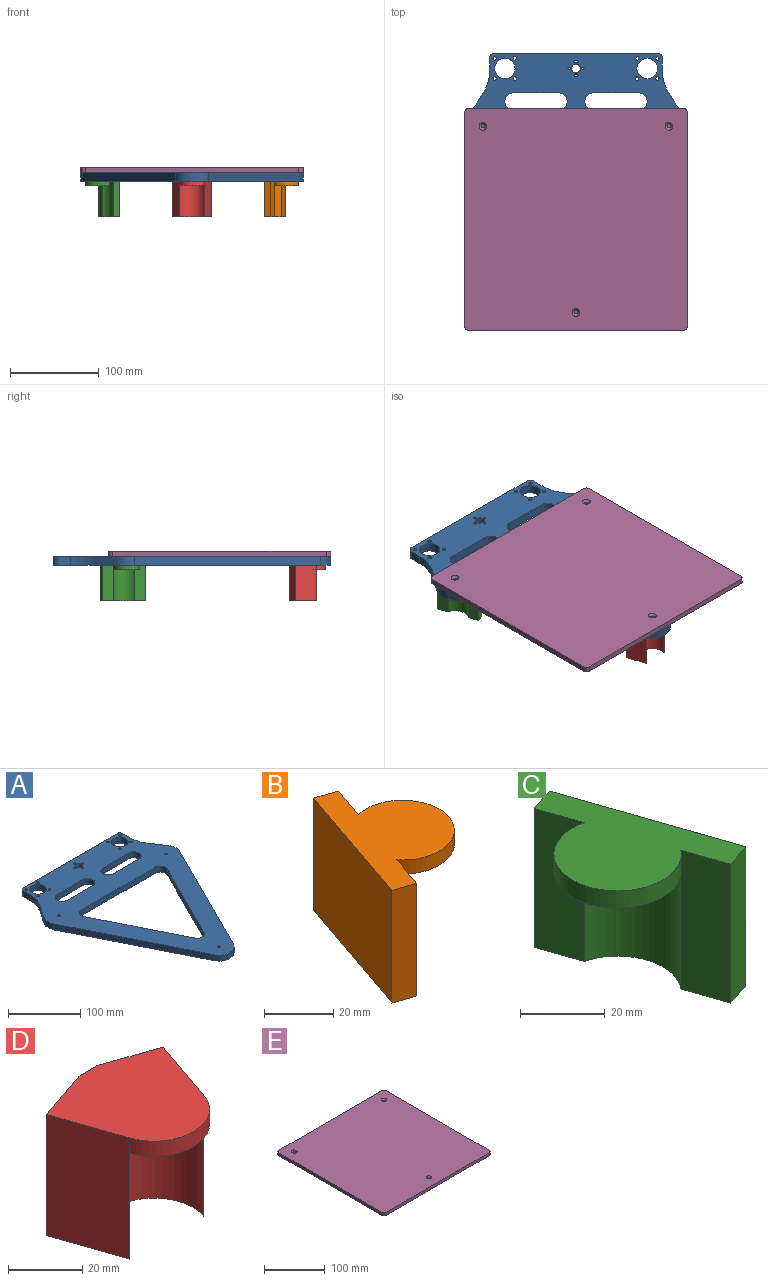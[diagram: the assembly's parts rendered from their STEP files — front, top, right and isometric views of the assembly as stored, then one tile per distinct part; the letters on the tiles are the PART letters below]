
ASSEMBLY  parts=5 mates=4
PART A: 48 faces, bbox 250x311.5x10 mm
  f0: plane 184x10mm, normal (0,1,0), area 1840mm2, adj f1,f13,f46,f47
  f1: cylinder r=5mm len=10mm, axis (0,0,-1), area 78.5mm2, adj f0,f2,f46,f47
  f2: plane 13.79x10mm, normal (-1,0,0), area 137.9mm2, adj f1,f3,f46,f47
  f3: cylinder r=50mm len=27.84mm, axis (0,0,-1), area 295.3mm2, adj f2,f4,f46,f47
  f4: plane 23.95x16.06mm, normal (-0.83,0.56,0), area 288.4mm2, adj f3,f5,f46,f47
  f5: cylinder r=20.5mm len=20.58mm, axis (0,0,-1), area 216.1mm2, adj f4,f6,f46,f47
  f6: plane 209x104.5mm, normal (-0.89,-0.45,0), area 2336.7mm2, adj f5,f7,f46,f47
  f7: cylinder r=20.5mm len=36.67mm, axis (0,0,-1), area 453.9mm2, adj f6,f8,f46,f47
  f8: plane 209x104.5mm, normal (0.89,-0.45,0), area 2336.7mm2, adj f7,f9,f46,f47
  f9: cylinder r=20.5mm len=20.58mm, axis (0,0,-1), area 216.1mm2, adj f8,f10,f46,f47
  f10: plane 23.95x16.06mm, normal (0.83,0.56,0), area 288.4mm2, adj f9,f11,f46,f47
  f11: cylinder r=50mm len=27.84mm, axis (0,0,-1), area 295.3mm2, adj f10,f12,f46,f47
  f12: plane 13.79x10mm, normal (1,0,0), area 137.9mm2, adj f11,f13,f46,f47
  f13: cylinder r=5mm len=10mm, axis (0,0,-1), area 78.5mm2, adj f0,f12,f46,f47
  f14: cylinder r=10mm len=14.47mm, axis (0,0,-1), area 203.4mm2, adj f15,f25,f46,f47
  f15: plane 143.84x71.92mm, normal (-0.89,0.45,0), area 1608.2mm2, adj f14,f16,f46,f47
  f16: cylinder r=10mm len=17.89mm, axis (0,0,-1), area 221.4mm2, adj f15,f17,f46,f47
  f17: plane 143.84x71.92mm, normal (0.89,0.45,0), area 1608.2mm2, adj f16,f18,f46,f47
  f18: cylinder r=10mm len=14.47mm, axis (0,0,-1), area 203.4mm2, adj f17,f25,f46,f47
  f19: plane 50x10mm, normal (0,1,0), area 500mm2, adj f20,f26,f46,f47
  f20: cylinder r=10mm len=20mm, axis (0,0,-1), area 314.2mm2, adj f19,f21,f46,f47
  f21: plane 50x10mm, normal (0,-1,0), area 500mm2, adj f20,f26,f46,f47
  f22: cylinder r=10mm len=20mm, axis (0,0,-1), area 314.2mm2, adj f23,f27,f46,f47
  f23: plane 50x10mm, normal (0,-1,0), area 500mm2, adj f22,f24,f46,f47
  f24: cylinder r=10mm len=20mm, axis (0,0,-1), area 314.2mm2, adj f23,f27,f46,f47
  f25: plane 143.84x10mm, normal (0,-1,0), area 1438.4mm2, adj f14,f18,f46,f47
  f26: cylinder r=10mm len=20mm, axis (0,0,-1), area 314.2mm2, adj f19,f21,f46,f47
  f27: plane 50x10mm, normal (0,1,0), area 500mm2, adj f22,f24,f46,f47
  f28: cylinder r=11.5mm len=23mm, axis (0,0,-1), area 722.6mm2, adj f46,f47
  f29: cylinder r=11.5mm len=23mm, axis (0,0,-1), area 722.6mm2, adj f46,f47
  f30: cylinder r=2mm len=10mm, axis (0,0,-1), area 125.7mm2, adj f46,f47
  f31: cylinder r=2mm len=10mm, axis (0,0,-1), area 125.7mm2, adj f46,f47
  f32: cylinder r=2mm len=10mm, axis (0,0,-1), area 125.7mm2, adj f46,f47
  f33: cylinder r=2mm len=10mm, axis (0,0,-1), area 125.7mm2, adj f46,f47
  f34: cylinder r=2mm len=10mm, axis (0,0,-1), area 125.7mm2, adj f46,f47
  f35: cylinder r=2mm len=10mm, axis (0,0,-1), area 125.7mm2, adj f46,f47
  f36: cylinder r=2mm len=10mm, axis (0,0,-1), area 125.7mm2, adj f46,f47
  f37: cylinder r=2mm len=10mm, axis (0,0,-1), area 125.7mm2, adj f46,f47
  f38: cylinder r=2mm len=10mm, axis (0,0,-1), area 125.7mm2, adj f46,f47
  f39: cylinder r=2mm len=10mm, axis (0,0,-1), area 125.7mm2, adj f46,f47
  f40: cylinder r=2mm len=10mm, axis (0,0,-1), area 125.7mm2, adj f46,f47
  f41: cylinder r=5mm len=10mm, axis (0,0,-1), area 314.2mm2, adj f46,f47
  f42: cylinder r=1.5mm len=10mm, axis (0,0,-1), area 94.2mm2, adj f46,f47
  f43: cylinder r=1.5mm len=10mm, axis (0,0,-1), area 94.2mm2, adj f46,f47
  f44: cylinder r=1.5mm len=10mm, axis (0,0,-1), area 94.2mm2, adj f46,f47
  f45: cylinder r=1.5mm len=10mm, axis (0,0,-1), area 94.2mm2, adj f46,f47
  f46: plane 311.5x250mm, normal (0,0,1), area 30515.8mm2, adj f0,f1,f2,f3,f4,f5,f6,f7
  f47: plane 311.5x250mm, normal (0,0,-1), area 30515.8mm2, adj f0,f1,f2,f3,f4,f5,f6,f7
PART B: 10 faces, bbox 38.5x51.4x40 mm
  f0: cylinder r=15mm len=30mm, axis (0,0,1), area 320mm2, adj f1,f2,f4,f8
  f1: plane 30x30mm, normal (0,0,-1), area 706.9mm2, adj f0,f3
  f2: plane 51.38x38.5mm, normal (0,0,1), area 994.1mm2, adj f0,f4,f5,f6,f7,f8
  f3: cylinder r=15mm len=35mm, axis (0,0,1), area 1058.7mm2, adj f1,f4,f8,f9
  f4: plane 40x12.39mm, normal (0.95,-0.32,0), area 524mm2, adj f0,f2,f3,f5,f9
  f5: plane 40x7.57mm, normal (0.32,0.95,0), area 320mm2, adj f2,f4,f6,f9
  f6: plane 48.78x40mm, normal (-0.95,0.32,0), area 2063mm2, adj f2,f5,f7,f9
  f7: plane 40x7.57mm, normal (-0.32,-0.95,0), area 320mm2, adj f2,f6,f8,f9
  f8: plane 40x12.39mm, normal (0.95,-0.32,0), area 524mm2, adj f0,f2,f3,f7,f9
  f9: plane 51.38x24.31mm, normal (0,0,-1), area 287.3mm2, adj f3,f4,f5,f6,f7,f8
PART C: 10 faces, bbox 38.5x51.4x40 mm
  f0: cylinder r=15mm len=30mm, axis (0,0,1), area 320mm2, adj f1,f2,f4,f5
  f1: plane 30x30mm, normal (0,0,-1), area 706.9mm2, adj f0,f3
  f2: plane 51.38x38.5mm, normal (0,0,1), area 994.1mm2, adj f0,f4,f5,f6,f7,f8
  f3: cylinder r=15mm len=35mm, axis (0,0,1), area 1058.7mm2, adj f1,f4,f5,f9
  f4: plane 40x12.39mm, normal (-0.95,-0.32,0), area 524mm2, adj f0,f2,f3,f8,f9
  f5: plane 40x12.39mm, normal (-0.95,-0.32,0), area 524mm2, adj f0,f2,f3,f6,f9
  f6: plane 40x7.57mm, normal (0.32,-0.95,0), area 320mm2, adj f2,f5,f7,f9
  f7: plane 48.78x40mm, normal (0.95,0.32,0), area 2063mm2, adj f2,f6,f8,f9
  f8: plane 40x7.57mm, normal (-0.32,0.95,0), area 320mm2, adj f2,f4,f7,f9
  f9: plane 51.38x24.31mm, normal (0,0,-1), area 287.3mm2, adj f3,f4,f5,f6,f7,f8
PART D: 10 faces, bbox 44.6x40.3x40 mm
  f0: plane 30x30mm, normal (0,0,-1), area 706.9mm2, adj f1,f8
  f1: cylinder r=15mm len=28.38mm, axis (0,0,1), area 186mm2, adj f0,f2,f6,f7
  f2: plane 40x23.65mm, normal (0.95,-0.32,0), area 1000mm2, adj f1,f3,f7,f8,f9
  f3: plane 40x18.92mm, normal (0.32,0.95,0), area 800mm2, adj f2,f4,f7,f9
  f4: plane 40x6.77mm, normal (0,1,0), area 270.9mm2, adj f3,f5,f7,f9
  f5: plane 40x18.92mm, normal (-0.32,0.95,0), area 800mm2, adj f4,f6,f7,f9
  f6: plane 40x23.65mm, normal (-0.95,-0.32,0), area 1000mm2, adj f1,f5,f7,f8,f9
  f7: plane 44.61x40.27mm, normal (0,0,1), area 1239.6mm2, adj f1,f2,f3,f4,f5,f6
  f8: cylinder r=15mm len=35mm, axis (0,0,1), area 1996.5mm2, adj f0,f2,f6,f9
  f9: plane 44.61x30.14mm, normal (0,0,-1), area 532.7mm2, adj f2,f3,f4,f5,f6,f8
PART E: 16 faces, bbox 250x250x6 mm
  f0: cylinder r=5mm len=6mm, axis (0,0,1), area 47.1mm2, adj f1,f7,f8,f9
  f1: plane 240x6mm, normal (0,-1,0), area 1440mm2, adj f0,f2,f8,f9
  f2: cylinder r=5mm len=6mm, axis (0,0,1), area 47.1mm2, adj f1,f3,f8,f9
  f3: plane 240x6mm, normal (1,0,0), area 1440mm2, adj f2,f4,f8,f9
  f4: cylinder r=5mm len=6mm, axis (0,0,1), area 47.1mm2, adj f3,f5,f8,f9
  f5: plane 240x6mm, normal (0,1,0), area 1440mm2, adj f4,f6,f8,f9
  f6: cylinder r=5mm len=6mm, axis (0,0,1), area 47.1mm2, adj f5,f7,f8,f9
  f7: plane 240x6mm, normal (-1,0,0), area 1440mm2, adj f0,f6,f8,f9
  f8: plane 250x250mm, normal (0,0,-1), area 62432.9mm2, adj f0,f1,f2,f3,f4,f5,f6,f7
  f9: plane 250x250mm, normal (0,0,1), area 62289.4mm2, adj f0,f1,f2,f3,f4,f5,f6,f7
  f10: cylinder r=2.2mm len=4.4mm, axis (0,0,1), area 51.4mm2, adj f8,f11
  f11: cone r=2.2mm half-angle=45deg, axis (0,0,1), area 67.7mm2, adj f9,f10
  f12: cylinder r=2.2mm len=4.4mm, axis (0,0,1), area 51.4mm2, adj f8,f13
  f13: cone r=2.2mm half-angle=45deg, axis (0,0,1), area 67.7mm2, adj f9,f12
  f14: cylinder r=2.2mm len=4.4mm, axis (0,0,1), area 51.4mm2, adj f8,f15
  f15: cone r=2.2mm half-angle=45deg, axis (0,0,1), area 67.7mm2, adj f9,f14
PLACE A t=(7.83,47.22,0.1)mm
PLACE B t=(7.83,-2.83,0.1)mm
PLACE C t=(7.83,-2.83,0.1)mm
PLACE D t=(7.83,-2.83,0.1)mm
PLACE E t=(4.4,-32.43,16.1)mm
MATE fastened B.f0 <-> E.f12  axis (0,0,1) through (112.33,117.75,0.1)mm
MATE fastened A.f32 <-> E.f14  axis (0,0,1) through (7.83,-91.25,10.1)mm
MATE fastened C.f0 <-> E.f10  axis (0,0,1) through (-96.67,117.75,0.1)mm
MATE fastened D.f1 <-> E.f14  axis (0,0,1) through (7.83,-91.25,0.1)mm
